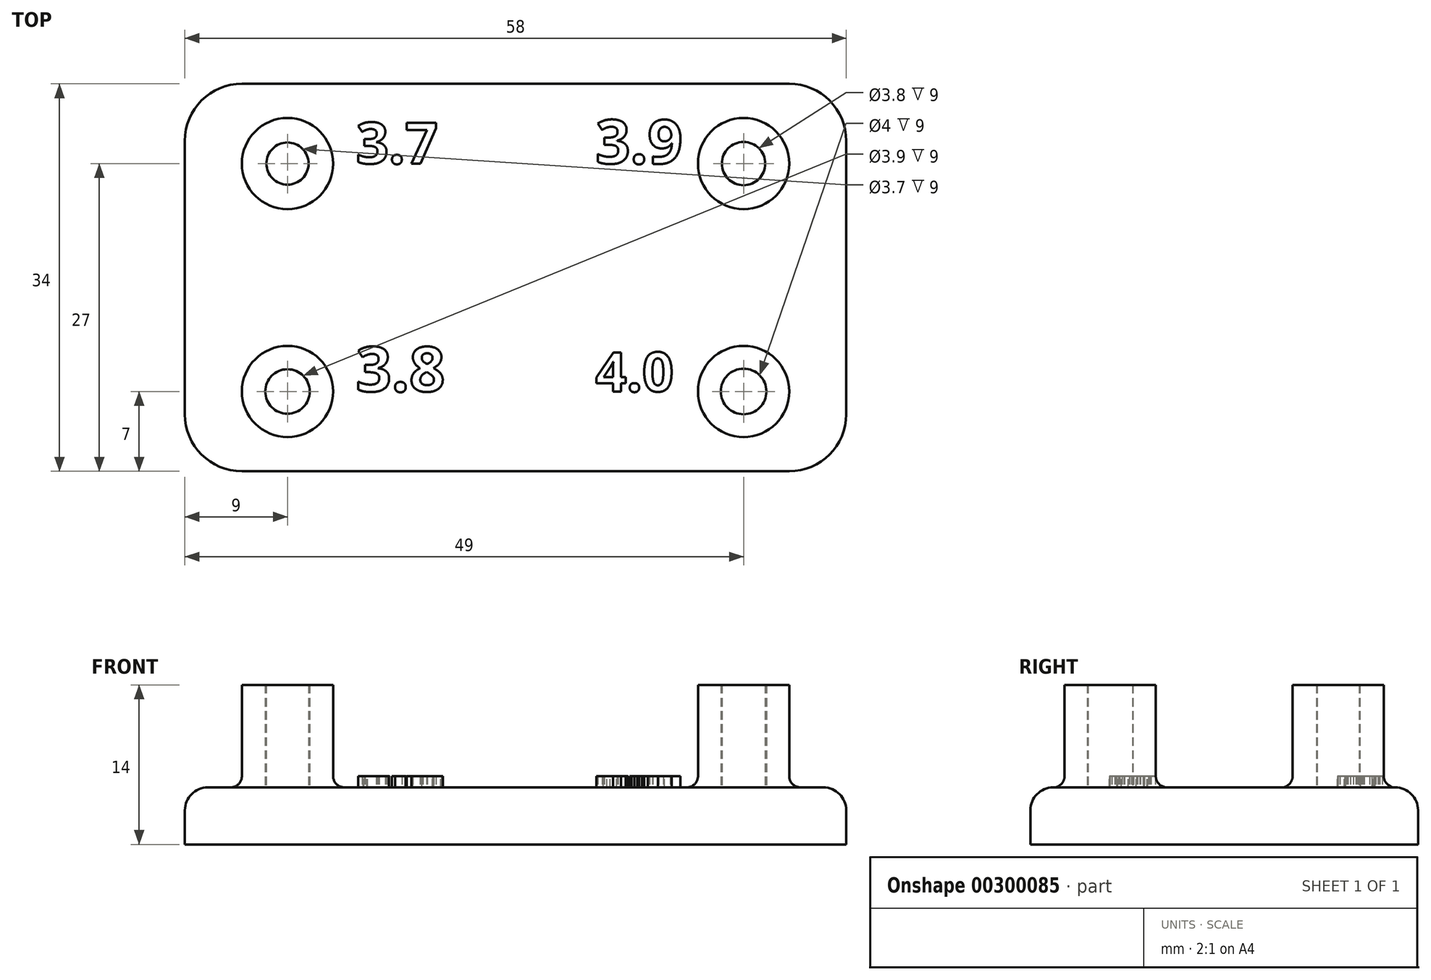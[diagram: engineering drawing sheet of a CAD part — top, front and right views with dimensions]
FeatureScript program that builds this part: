
annotation { "Feature Type Name" : "Feature", "Feature Type Description" : "" }
export const myFeature = defineFeature(function(context is Context, id is Id, definition is map)
    precondition{}
    {
        {
            var Q0;
            Q0=qCreatedBy(makeId("Top.planeOp"),FACE);
            var sketch = newSketch(context, id + "F0", { "sketchPlane" : qUnion([Q0])});
            skCircle(sketch, "E0", {"center": v(-20, 10) * mm, "radius": 4 * mm});
            skCircle(sketch, "E1", {"center": v(-20, -10) * mm, "radius": 4 * mm});
            skCircle(sketch, "E2", {"center": v(20, -10) * mm, "radius": 4 * mm});
            skCircle(sketch, "E3", {"center": v(20, 10) * mm, "radius": 4 * mm});
            skCircle(sketch, "E4", {"center": v(-20, 10) * mm, "radius": 1.85 * mm});
            skCircle(sketch, "E5", {"center": v(20, 10) * mm, "radius": 1.9 * mm});
            skCircle(sketch, "E6", {"center": v(-20, -10) * mm, "radius": 1.95 * mm});
            skCircle(sketch, "E7", {"center": v(20, -10) * mm, "radius": 2 * mm});
            skSolve(sketch);
        }
        {
            var Q0;
            Q0 = qSketchRegion(id + "F0", true);
            extrude(context, id + "F1", {"entities" : qUnion([Q0]), "depth" : 12 * mm});
        }
        {
            var Q0;
            Q0=qCreatedBy(makeId("Top.planeOp"),FACE);
            var sketch = newSketch(context, id + "F2", { "sketchPlane" : qUnion([Q0])});
            skLineSegment(sketch, "E8.bottom", {"start": v(29, -17) * mm, "end": v(-29, -17) * mm});
            skLineSegment(sketch, "E8.top", {"start": v(29, 17) * mm, "end": v(-29, 17) * mm});
            skLineSegment(sketch, "E8.left", {"start": v(29, -17) * mm, "end": v(29, 17) * mm});
            skLineSegment(sketch, "E8.right", {"start": v(-29, -17) * mm, "end": v(-29, 17) * mm});
            skPoint(sketch, "E8.middle", {"position": v(0, 0) * mm});
            skSolve(sketch);
        }
        {
            var Q0;
            Q0 = qSketchRegion(id + "F2", true);
            extrude(context, id + "F3", {"entities" : qUnion([Q0]), "depth" : 5 * mm});
        }
        {
            var Q0;
            Q0=makeQuery(id+"F1.opExtrude","SWEPT_BODY",BODY,{"disambiguationData":[OSD([sQuery(id+"F0.wireOp",EDGE,"E3"),sQuery(id+"F0.wireOp",EDGE,"E5")])]});
            var Q1;
            Q1=makeQuery(id+"F1.opExtrude","SWEPT_BODY",BODY,{"disambiguationData":[OSD([sQuery(id+"F0.wireOp",EDGE,"E2"),sQuery(id+"F0.wireOp",EDGE,"E7")])]});
            var Q2;
            Q2=makeQuery(id+"F1.opExtrude","SWEPT_BODY",BODY,{"disambiguationData":[OSD([sQuery(id+"F0.wireOp",EDGE,"E1"),sQuery(id+"F0.wireOp",EDGE,"E6")])]});
            var Q3;
            Q3=makeQuery(id+"F1.opExtrude","SWEPT_BODY",BODY,{"disambiguationData":[OSD([sQuery(id+"F0.wireOp",EDGE,"E0"),sQuery(id+"F0.wireOp",EDGE,"E4")])]});
            transform(context, id + "F4", {"entities" : qUnion([Q0, Q1, Q2, Q3]), "transformType" : TransformType.TRANSLATION_3D, "dx" : 0 * mm, "dy" : 0 * mm, "dz" : 2 * mm, "makeCopy" : false});
        }
        {
            var Q0;
            Q0=makeQuery(id+"F3.opExtrude","SWEPT_EDGE",EDGE,{"disambiguationData":[OSD([sQuery(id+"F2.wireOp",EDGE,"E8.bottom"),sQuery(id+"F2.wireOp",EDGE,"E8.left")])]});
            var Q1;
            Q1=makeQuery(id+"F3.opExtrude","SWEPT_EDGE",EDGE,{"disambiguationData":[OSD([sQuery(id+"F2.wireOp",EDGE,"E8.bottom"),sQuery(id+"F2.wireOp",EDGE,"E8.right")])]});
            var Q2;
            Q2=makeQuery(id+"F3.opExtrude","SWEPT_EDGE",EDGE,{"disambiguationData":[OSD([sQuery(id+"F2.wireOp",EDGE,"E8.top"),sQuery(id+"F2.wireOp",EDGE,"E8.right")])]});
            var Q3;
            Q3=makeQuery(id+"F3.opExtrude","SWEPT_EDGE",EDGE,{"disambiguationData":[OSD([sQuery(id+"F2.wireOp",EDGE,"E8.top"),sQuery(id+"F2.wireOp",EDGE,"E8.left")])]});
            fillet(context, id + "F5", {"entities" : qUnion([Q0, Q1, Q2, Q3]), "radius" : 5 * mm, "tangentPropagation" : true, "allowEdgeOverflow" : false});
        }
        {
            var Q0;
            Q0=qCreatedBy(makeId("Top.planeOp"),FACE);
            var sketch = newSketch(context, id + "F6", { "sketchPlane" : qUnion([Q0])});
            skLineSegment(sketch, "E9", {"start": v(0, 0) * mm, "end": v(-14, 0) * mm});
            skLineSegment(sketch, "E10", {"start": v(-14, 0) * mm, "end": v(-14, 10) * mm});
            skLineSegment(sketch, "E11", {"start": v(-14, 10) * mm, "end": v(-14, -10) * mm});
            skLineSegment(sketch, "E12", {"start": v(0, 0) * mm, "end": v(14, 0) * mm});
            skLineSegment(sketch, "E13", {"start": v(14, 0) * mm, "end": v(14, 10) * mm});
            skLineSegment(sketch, "E14", {"start": v(14, 10) * mm, "end": v(14, -10) * mm});
            skText(sketch, "E15", { "text": "3.7", "fontName": "OpenSans-Bold.ttf"});
            skText(sketch, "E16", { "text": "3.8", "fontName": "OpenSans-Bold.ttf"});
            skLineSegment(sketch, "E17", {"start": v(14, 10) * mm, "end": v(7, 10) * mm});
            skLineSegment(sketch, "E18", {"start": v(14, -10) * mm, "end": v(7, -10) * mm});
            skText(sketch, "E19", { "text": "3.9", "fontName": "OpenSans-Bold.ttf"});
            skText(sketch, "E20", { "text": "4.0", "fontName": "OpenSans-Bold.ttf"});
            const initialGuessF6  = {"E15": [-0.014, 0.01, 1, 0, 0.00363], "E16": [-0.014, -0.01, 1, 0, 0.00394], "E19": [0.007, 0.01, 1, 0, 0.00386], "E20": [0.007, -0.01, 1, 0, 0.00346]};
            skSetInitialGuess(sketch, initialGuessF6);
            skSolve(sketch);
        }
        {
            var Q0;
            Q0 = qSketchRegion(id + "F6", true);
            extrude(context, id + "F7", {"entities" : qUnion([Q0]), "operationType" : NewBodyOperationType.ADD, "depth" : 6 * mm});
        }
        {
            var Q0;
            Q0=makeQuery(id+"F1.opExtrude","SWEPT_BODY",BODY,{"disambiguationData":[OSD([sQuery(id+"F0.wireOp",EDGE,"E0"),sQuery(id+"F0.wireOp",EDGE,"E4")])]});
            var Q1;
            Q1=makeQuery(id+"F1.opExtrude","SWEPT_BODY",BODY,{"disambiguationData":[OSD([sQuery(id+"F0.wireOp",EDGE,"E1"),sQuery(id+"F0.wireOp",EDGE,"E6")])]});
            var Q2;
            Q2=makeQuery(id+"F1.opExtrude","SWEPT_BODY",BODY,{"disambiguationData":[OSD([sQuery(id+"F0.wireOp",EDGE,"E2"),sQuery(id+"F0.wireOp",EDGE,"E7")])]});
            var Q3;
            Q3=makeQuery(id+"F1.opExtrude","SWEPT_BODY",BODY,{"disambiguationData":[OSD([sQuery(id+"F0.wireOp",EDGE,"E3"),sQuery(id+"F0.wireOp",EDGE,"E5")])]});
            var Q4;
            Q4=makeQuery(id+"F3.opExtrude","SWEPT_BODY",BODY,{"disambiguationData":[OSD([sQuery(id+"F2.wireOp",EDGE,"E8.bottom"),sQuery(id+"F2.wireOp",EDGE,"E8.top"),sQuery(id+"F2.wireOp",EDGE,"E8.left"),sQuery(id+"F2.wireOp",EDGE,"E8.right")])]});
            booleanBodies(context, id + "F8", {"operationType" : BooleanOperationType.UNION, "tools" : qUnion([Q0, Q1, Q2, Q3, Q4])});
        }
        {
            var Q0;
            Q0=makeQuery(id+"F3.opExtrude","CAP_EDGE",EDGE,{"disambiguationData":[OSD([sQuery(id+"F2.wireOp",EDGE,"E8.bottom")])],"isStart":false});
            fillet(context, id + "F9", {"entities" : qUnion([Q0]), "radius" : 2 * mm, "tangentPropagation" : true, "allowEdgeOverflow" : false});
        }
        {
            var Q0;
            {var subQ0=sQuery(id+"F2.wireOp",EDGE,"E8.left");var subQ1=sQuery(id+"F2.wireOp",EDGE,"E8.right");var subQ2=sQuery(id+"F2.wireOp",EDGE,"E8.bottom");var subQ3=sQuery(id+"F2.wireOp",EDGE,"E8.top");Q0=makeQuery(id+"F8.opBoolean","INTERSECT",EDGE,{"derivedFrom":[makeQuery(id+"F1.opExtrude","SWEPT_FACE",FACE,{"disambiguationData":[OSD([sQuery(id+"F0.wireOp",EDGE,"E1")])]}),makeQuery(id+"F7.boolean.opBoolean","SPLIT",FACE,{"disambiguationData":[TD([makeQuery(id+"F3.opExtrude","SWEPT_FACE",FACE,{"disambiguationData":[OSD([subQ2])]})])],"derivedFrom":makeQuery(id+"F3.opExtrude","CAP_FACE",FACE,{"disambiguationData":[OSD([subQ2,subQ3,subQ0,subQ1])],"isStart":false})})]});}
            var Q1;
            {var subQ0=sQuery(id+"F2.wireOp",EDGE,"E8.left");var subQ1=sQuery(id+"F2.wireOp",EDGE,"E8.right");var subQ2=sQuery(id+"F2.wireOp",EDGE,"E8.bottom");var subQ3=sQuery(id+"F2.wireOp",EDGE,"E8.top");Q1=makeQuery(id+"F8.opBoolean","INTERSECT",EDGE,{"derivedFrom":[makeQuery(id+"F1.opExtrude","SWEPT_FACE",FACE,{"disambiguationData":[OSD([sQuery(id+"F0.wireOp",EDGE,"E0")])]}),makeQuery(id+"F7.boolean.opBoolean","SPLIT",FACE,{"disambiguationData":[TD([makeQuery(id+"F3.opExtrude","SWEPT_FACE",FACE,{"disambiguationData":[OSD([subQ2])]})])],"derivedFrom":makeQuery(id+"F3.opExtrude","CAP_FACE",FACE,{"disambiguationData":[OSD([subQ2,subQ3,subQ0,subQ1])],"isStart":false})})]});}
            var Q2;
            {var subQ0=sQuery(id+"F2.wireOp",EDGE,"E8.left");var subQ1=sQuery(id+"F2.wireOp",EDGE,"E8.right");var subQ2=sQuery(id+"F2.wireOp",EDGE,"E8.bottom");var subQ3=sQuery(id+"F2.wireOp",EDGE,"E8.top");Q2=makeQuery(id+"F8.opBoolean","INTERSECT",EDGE,{"derivedFrom":[makeQuery(id+"F1.opExtrude","SWEPT_FACE",FACE,{"disambiguationData":[OSD([sQuery(id+"F0.wireOp",EDGE,"E2")])]}),makeQuery(id+"F7.boolean.opBoolean","SPLIT",FACE,{"disambiguationData":[TD([makeQuery(id+"F3.opExtrude","SWEPT_FACE",FACE,{"disambiguationData":[OSD([subQ2])]})])],"derivedFrom":makeQuery(id+"F3.opExtrude","CAP_FACE",FACE,{"disambiguationData":[OSD([subQ2,subQ3,subQ0,subQ1])],"isStart":false})})]});}
            var Q3;
            {var subQ0=sQuery(id+"F2.wireOp",EDGE,"E8.left");var subQ1=sQuery(id+"F2.wireOp",EDGE,"E8.right");var subQ2=sQuery(id+"F2.wireOp",EDGE,"E8.bottom");var subQ3=sQuery(id+"F2.wireOp",EDGE,"E8.top");Q3=makeQuery(id+"F8.opBoolean","INTERSECT",EDGE,{"derivedFrom":[makeQuery(id+"F1.opExtrude","SWEPT_FACE",FACE,{"disambiguationData":[OSD([sQuery(id+"F0.wireOp",EDGE,"E3")])]}),makeQuery(id+"F7.boolean.opBoolean","SPLIT",FACE,{"disambiguationData":[TD([makeQuery(id+"F3.opExtrude","SWEPT_FACE",FACE,{"disambiguationData":[OSD([subQ2])]})])],"derivedFrom":makeQuery(id+"F3.opExtrude","CAP_FACE",FACE,{"disambiguationData":[OSD([subQ2,subQ3,subQ0,subQ1])],"isStart":false})})]});}
            fillet(context, id + "F10", {"entities" : qUnion([Q0, Q1, Q2, Q3]), "radius" : 1 * mm, "tangentPropagation" : true, "allowEdgeOverflow" : false});
        }
    });
